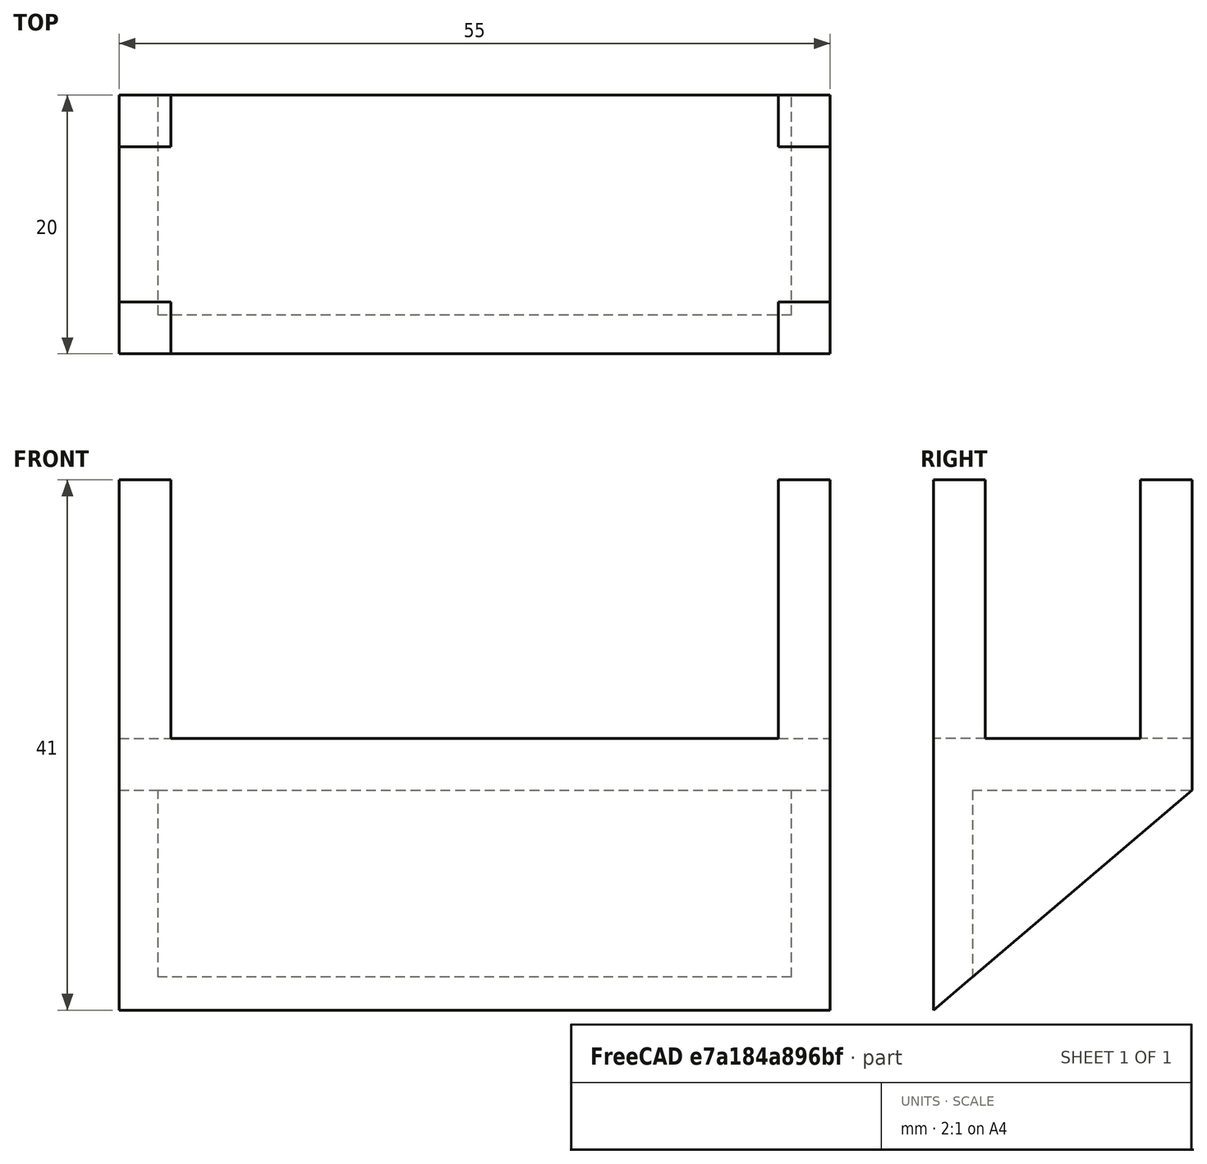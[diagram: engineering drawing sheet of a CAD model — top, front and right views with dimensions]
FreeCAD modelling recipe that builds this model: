
FCSTD DOCUMENT  (FreeCAD 0.19R)
Label: Hachimalbench
License: All rights reserved
LicenseURL: http://en.wikipedia.org/wiki/All_rights_reserved
objects: Sketcher::SketchObject×6, PartDesign::Pad×4, PartDesign::Mirrored×2, PartDesign::Pocket×1, PartDesign::Body×1, Mesh::Feature×1
note: 19 computed .brp shape members not serialized (recipe doc carries the construction recipe); baked Part::Feature solids carry a one-line shape summary decoded from their .brp

FEATURE [Sketcher::SketchObject] Sketch
  FullyConstrained = true
  MapMode = 5
  Support = -> [XY_Plane]
  sketch-geometry (4):
    g0: LineSegment StartX=-27.5 StartY=10 StartZ=0 EndX=27.5 EndY=10 EndZ=0
    g1: LineSegment StartX=27.5 StartY=10 StartZ=0 EndX=27.5 EndY=-10 EndZ=0
    g2: LineSegment StartX=27.5 StartY=-10 StartZ=0 EndX=-27.5 EndY=-10 EndZ=0
    g3: LineSegment StartX=-27.5 StartY=-10 StartZ=0 EndX=-27.5 EndY=10 EndZ=0
  constraints (11):
    c: Coincident(g0,g1)
    c: Coincident(g1,g2)
    c: Coincident(g2,g3)
    c: Coincident(g3,g0)
    c: Horizontal(g0)
    c: Horizontal(g2)
    c: Vertical(g1)
    c: Vertical(g3)
    c: Symmetric(g1,g0,g-1)
    c: Distance(g1) = 20
    c: Distance(g0) = 55
FEATURE [PartDesign::Pad] Pad
  Direction = (1,1,1)
  Length = 4
  Length2 = 100
  Profile = -> Sketch
  Type = 0
FEATURE [Sketcher::SketchObject] Sketch001
  ExternalGeometry = -> [Pad]
  FullyConstrained = true
  MapMode = 5
  Placement = pos=(0,0,4) rot=(0,0,1;0rad)
  Support = -> [Pad]
  sketch-geometry (8):
    g0: LineSegment StartX=23.5 StartY=-10 StartZ=0 EndX=27.5 EndY=-10 EndZ=0
    g1: LineSegment StartX=27.5 StartY=-10 StartZ=0 EndX=27.5 EndY=-6 EndZ=0
    g2: LineSegment StartX=27.5 StartY=-6 StartZ=0 EndX=23.5 EndY=-6 EndZ=0
    g3: LineSegment StartX=23.5 StartY=-6 StartZ=0 EndX=23.5 EndY=-10 EndZ=0
    g4: LineSegment StartX=23.5 StartY=6 StartZ=0 EndX=27.5 EndY=6 EndZ=0
    g5: LineSegment StartX=27.5 StartY=6 StartZ=0 EndX=27.5 EndY=10 EndZ=0
    g6: LineSegment StartX=27.5 StartY=10 StartZ=0 EndX=23.5 EndY=10 EndZ=0
    g7: LineSegment StartX=23.5 StartY=10 StartZ=0 EndX=23.5 EndY=6 EndZ=0
  constraints (22):
    c: Coincident(g0,g1)
    c: Coincident(g1,g2)
    c: Coincident(g2,g3)
    c: Coincident(g3,g0)
    c: Horizontal(g0)
    c: Horizontal(g2)
    c: Vertical(g1)
    c: Vertical(g3)
    c: Coincident(g4,g5)
    c: Coincident(g5,g6)
    c: Coincident(g6,g7)
    c: Coincident(g7,g4)
    c: Horizontal(g4)
    c: Horizontal(g6)
    c: Vertical(g5)
    c: Vertical(g7)
    c: Equal(g7,g1)
    c: Equal(g1,g0)
    c: Equal(g0,g4)
    c: Distance(g4) = 4
    c: Coincident(g0,g-4)
    c: Coincident(g5,g-4)
FEATURE [PartDesign::Pad] Pad001
  BaseFeature = -> Pad
  Direction = (1,1,1)
  Length = 20
  Length2 = 100
  Profile = -> Sketch001
  Type = 0
FEATURE [PartDesign::Mirrored] Mirrored
  BaseFeature = -> Pad001
  MirrorPlane = -> Sketch001 [V_Axis]
  Originals = -> [Pad001]
FEATURE [Sketcher::SketchObject] Sketch002
  FullyConstrained = true
  MapMode = 5
  Placement = pos=(0,0,0) rot=(1,0,0;3.14159rad)
  Support = -> [Mirrored]
FEATURE [Sketcher::SketchObject] Sketch003
  ExternalGeometry = -> [Mirrored]
  FullyConstrained = true
  MapMode = 5
  Placement = pos=(0,0,0) rot=(1,0,0;3.14159rad)
  Support = -> [Mirrored]
  sketch-geometry (4):
    g0: LineSegment StartX=-27.5 StartY=7 StartZ=0 EndX=27.5 EndY=7 EndZ=0
    g1: LineSegment StartX=27.5 StartY=7 StartZ=0 EndX=27.5 EndY=10 EndZ=0
    g2: LineSegment StartX=27.5 StartY=10 StartZ=0 EndX=-27.5 EndY=10 EndZ=0
    g3: LineSegment StartX=-27.5 StartY=10 StartZ=0 EndX=-27.5 EndY=7 EndZ=0
  constraints (10):
    c: Coincident(g0,g1)
    c: Coincident(g1,g2)
    c: Coincident(g2,g3)
    c: Coincident(g3,g0)
    c: Horizontal(g0)
    c: Vertical(g1)
    c: Vertical(g3)
    c: Distance(g1) = 3
    c: Coincident(g1,g-3)
    c: Coincident(g2,g-3)
FEATURE [PartDesign::Pad] Pad002
  BaseFeature = -> Mirrored
  Direction = (1,1,1)
  Length = 17
  Length2 = 100
  Profile = -> Sketch003
  Type = 0
FEATURE [Sketcher::SketchObject] Sketch004
  ExternalGeometry = -> [Pad002]
  FullyConstrained = false
  MapMode = 5
  Placement = pos=(-27.5,0,0) rot=(0.57735,-0.57735,-0.57735;2.0944rad)
  Support = -> [Pad002]
  sketch-geometry (3):
    g0: LineSegment StartX=-10 StartY=0 StartZ=0 EndX=7 EndY=-17 EndZ=0
    g1: LineSegment StartX=7 StartY=-17 StartZ=0 EndX=8.05557 EndY=0.977415 EndZ=0
    g2: LineSegment StartX=8.05557 StartY=0.977415 StartZ=0 EndX=-10 EndY=0 EndZ=0
  constraints (5):
    c: Coincident(g2,g1)
    c: Coincident(g0,g-3)
    c: Coincident(g1,g0)
    c: Coincident(g2,g-4)
    c: Coincident(g0,g2)
FEATURE [PartDesign::Pad] Pad003
  BaseFeature = -> Pad002
  Direction = (1,1,1)
  Length = 3
  Length2 = 100
  Profile = -> Sketch004
  Reversed = true
  Type = 0
FEATURE [PartDesign::Mirrored] Mirrored001
  BaseFeature = -> Pad003
  MirrorPlane = -> YZ_Plane
  Originals = -> [Pad003]
FEATURE [Sketcher::SketchObject] Sketch005
  ExternalGeometry = -> [Mirrored001]
  FullyConstrained = false
  MapMode = 5
  Placement = pos=(27.5,-6.1e-15,6.1e-15) rot=(0.57735,0.57735,0.57735;2.0944rad)
  Support = -> [Mirrored001]
  sketch-geometry (4):
    g0: LineSegment StartX=10 StartY=-5.3e-15 StartZ=0 EndX=-10 EndY=-17 EndZ=0
    g1: LineSegment StartX=-10 StartY=-17 StartZ=0 EndX=-6.44768 EndY=-20.0787 EndZ=0
    g2: LineSegment StartX=-6.44768 StartY=-20.0787 StartZ=0 EndX=18.4293 EndY=-10.7736 EndZ=0
    g3: LineSegment StartX=18.4293 StartY=-10.7736 StartZ=0 EndX=10 EndY=-5.3e-15 EndZ=0
  constraints (6):
    c: Coincident(g-3,g0)
    c: Coincident(g0,g-4)
    c: Coincident(g0,g1)
    c: Coincident(g1,g2)
    c: Coincident(g2,g3)
    c: Coincident(g3,g0)
FEATURE [PartDesign::Pocket] Pocket
  BaseFeature = -> Mirrored001
  Length = 5
  Length2 = 100
  Profile = -> Sketch005
  Type = 1
FEATURE [PartDesign::Body] Body
  Group = -> [Sketch,Pad,Sketch001,Pad001,Mirrored,Sketch002,Sketch003,Pad002,Sketch004,Pad003,Mirrored001,Sketch005,Pocket]
  Origin = -> Origin
  Tip = -> Pocket
FEATURE [Mesh::Feature] Mesh  label="Pocket (Meshed)"
